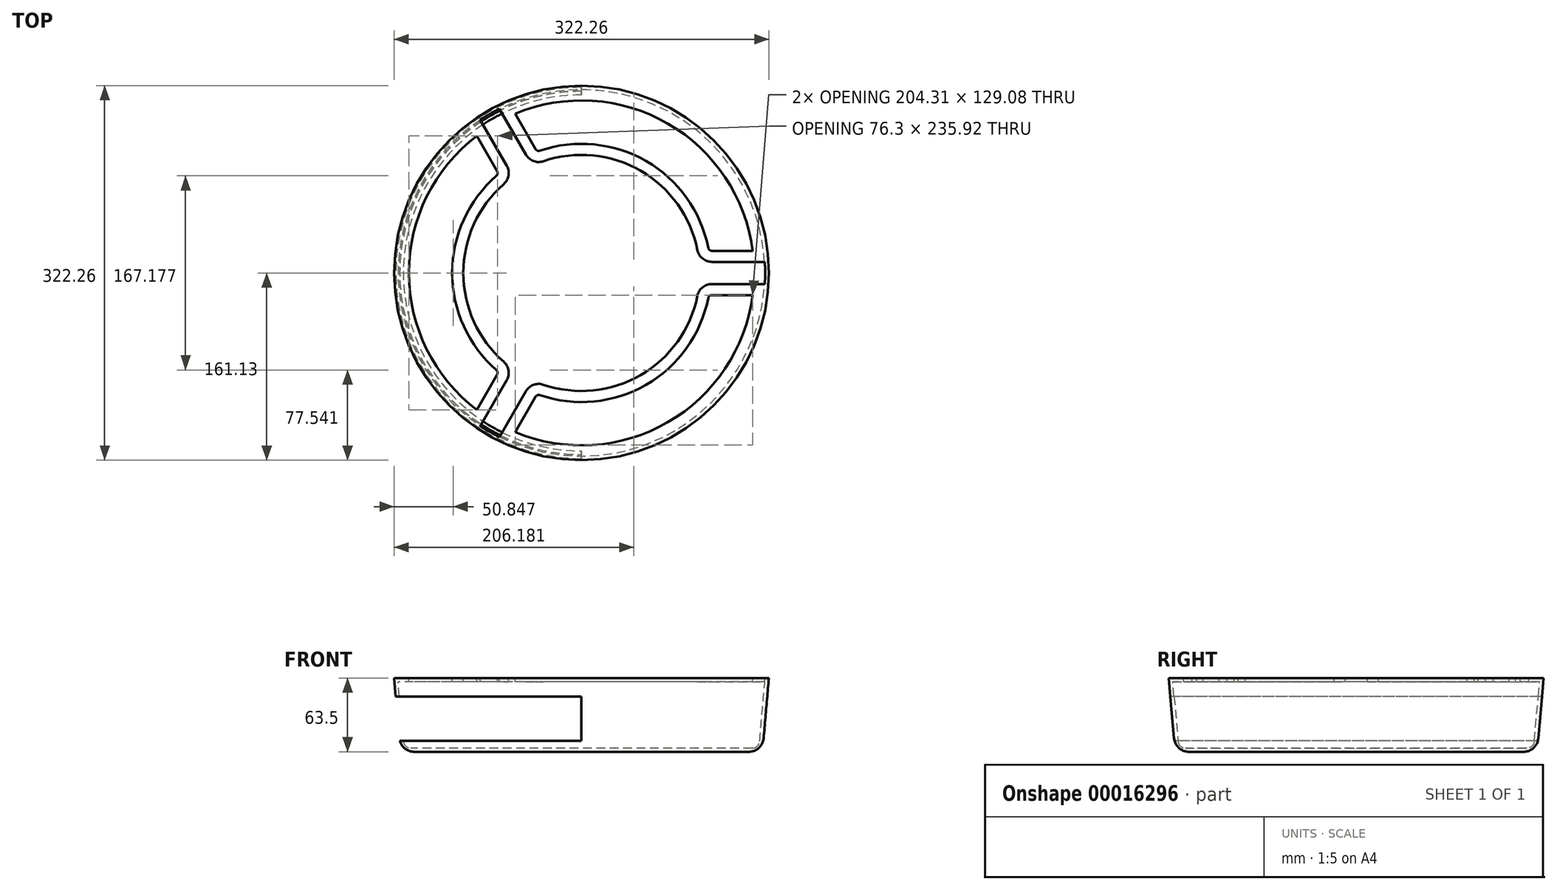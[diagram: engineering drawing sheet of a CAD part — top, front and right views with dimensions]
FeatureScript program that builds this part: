
annotation { "Feature Type Name" : "Feature", "Feature Type Description" : "" }
export const myFeature = defineFeature(function(context is Context, id is Id, definition is map)
    precondition{}
    {
        {
            var Q0;
            Q0=qCreatedBy(makeId("Top.planeOp"),FACE);
            var sketch = newSketch(context, id + "F0", { "sketchPlane" : qUnion([Q0])});
            skCircle(sketch, "E0", {"center": v(0, 0) * mm, "radius": 155.57 * mm});
            skSolve(sketch);
        }
        {
            var Q0;
            Q0 = qSketchRegion(id + "F0", true);
            extrude(context, id + "F1", {"entities" : qUnion([Q0]), "depth" : 63.5 * mm, "hasDraft" : true, "draftAngle" : 5 * degree});
        }
        {
            var Q0;
            Q0=makeQuery(id+"F1.opExtrude","CAP_FACE",FACE,{"disambiguationData":[OSD([sQuery(id+"F0.wireOp",EDGE,"E0")])],"isStart":false});
            shell(context, id + "F2", {"entities" : qUnion([Q0]), "thickness" : 3.17 * mm});
        }
        {
            var Q0;
            {var subQ0=sQuery(id+"F0.wireOp",EDGE,"E0");Q0=makeQuery(id+"F2.opShell","OFFSET_EDGE",EDGE,{"disambiguationData":[OSD([subQ0]),TDD([makeQuery(id+"F1.opExtrude","CAP_EDGE",EDGE,{"disambiguationData":[OSD([subQ0])],"isStart":true})])]});}
            fillet(context, id + "F3", {"entities" : qUnion([Q0]), "radius" : 6.35 * mm, "tangentPropagation" : true, "allowEdgeOverflow" : false});
        }
        {
            var Q0;
            Q0=makeQuery(id+"F1.opExtrude","CAP_EDGE",EDGE,{"disambiguationData":[OSD([sQuery(id+"F0.wireOp",EDGE,"E0")])],"isStart":true});
            fillet(context, id + "F4", {"entities" : qUnion([Q0]), "radius" : 12.7 * mm, "tangentPropagation" : true, "allowEdgeOverflow" : false});
        }
        {
            var Q0;
            Q0=makeQuery(id+"F1.opExtrude","CAP_FACE",FACE,{"disambiguationData":[OSD([sQuery(id+"F0.wireOp",EDGE,"E0")])],"isStart":false});
            var sketch = newSketch(context, id + "F5", { "sketchPlane" : qUnion([Q0])});
            skCircle(sketch, "E1", {"center": v(0, 0) * mm, "radius": 161.12 * mm});
            skLineSegment(sketch, "E2", {"start": v(161.12, 0) * mm, "end": v(161.13, 0) * mm});
            skLineSegment(sketch, "E3.1.0", {"start": v(-80.56, 139.54) * mm, "end": v(-80.57, 139.54) * mm});
            skLineSegment(sketch, "E3.2.0", {"start": v(-80.56, -139.54) * mm, "end": v(-80.57, -139.54) * mm});
            skArc(sketch, "E4", {"start": v(-66.94, 76.43) * mm, "mid": v(-101.6, 0) * mm, "end": v(-66.94, -76.43) * mm});
            skLineSegment(sketch, "E5.0", {"start": v(-47.81, 101.86) * mm, "end": v(-72.17, 144.06) * mm});
            skLineSegment(sketch, "E6.0", {"start": v(-64.3, 92.33) * mm, "end": v(-88.67, 134.53) * mm});
            skLineSegment(sketch, "E7.1.0", {"start": v(-64.3, -92.33) * mm, "end": v(-88.67, -134.53) * mm});
            skLineSegment(sketch, "E7.1.1", {"start": v(-47.81, -101.86) * mm, "end": v(-72.17, -144.06) * mm});
            skLineSegment(sketch, "E7.2.0", {"start": v(112.12, -9.52) * mm, "end": v(160.84, -9.52) * mm});
            skLineSegment(sketch, "E7.2.1", {"start": v(112.12, 9.52) * mm, "end": v(160.84, 9.52) * mm});
            skArc(sketch, "E8.trimOffspring", {"start": v(99.66, 19.76) * mm, "mid": v(50.8, 87.99) * mm, "end": v(-32.72, 96.19) * mm});
            skArc(sketch, "E9.trimOffspring", {"start": v(-32.72, -96.19) * mm, "mid": v(50.8, -87.99) * mm, "end": v(99.66, -19.76) * mm});
            skPoint(sketch, "E10.visualSharp", {"position": v(-58.83, -82.84) * mm});
            skArc(sketch, "E10.filletArc", {"start": v(-64.3, -92.33) * mm, "mid": v(-62.78, -83.91) * mm, "end": v(-66.94, -76.43) * mm});
            skPoint(sketch, "E11.visualSharp", {"position": v(101.15, -9.53) * mm});
            skArc(sketch, "E11.filletArc", {"start": v(112.12, -9.52) * mm, "mid": v(104.06, -12.41) * mm, "end": v(99.66, -19.76) * mm});
            skPoint(sketch, "E12.visualSharp", {"position": v(101.15, 9.52) * mm});
            skArc(sketch, "E12.filletArc", {"start": v(99.66, 19.76) * mm, "mid": v(104.06, 12.41) * mm, "end": v(112.12, 9.53) * mm});
            skPoint(sketch, "E13.visualSharp", {"position": v(-42.33, 92.36) * mm});
            skArc(sketch, "E13.filletArc", {"start": v(-47.81, 101.86) * mm, "mid": v(-41.28, 96.32) * mm, "end": v(-32.72, 96.19) * mm});
            skPoint(sketch, "E14.visualSharp", {"position": v(-58.83, 82.84) * mm});
            skArc(sketch, "E14.filletArc", {"start": v(-66.94, 76.43) * mm, "mid": v(-62.78, 83.91) * mm, "end": v(-64.3, 92.33) * mm});
            skPoint(sketch, "E15.visualSharp", {"position": v(-42.33, -92.36) * mm});
            skArc(sketch, "E15.filletArc", {"start": v(-32.72, -96.19) * mm, "mid": v(-41.28, -96.32) * mm, "end": v(-47.81, -101.86) * mm});
            skLineSegment(sketch, "E16.0", {"start": v(-72.56, 87.57) * mm, "end": v(-90.1, 117.96) * mm});
            skArc(sketch, "E16.1", {"start": v(-73.21, 83.6) * mm, "mid": v(-72.17, 85.47) * mm, "end": v(-72.56, 87.57) * mm});
            skArc(sketch, "E16.2", {"start": v(-73.21, 83.6) * mm, "mid": v(-111.13, 0) * mm, "end": v(-73.21, -83.6) * mm});
            skArc(sketch, "E16.3", {"start": v(-72.56, -87.57) * mm, "mid": v(-72.17, -85.47) * mm, "end": v(-73.21, -83.6) * mm});
            skLineSegment(sketch, "E16.4", {"start": v(-72.56, -87.57) * mm, "end": v(-90.1, -117.96) * mm});
            skLineSegment(sketch, "E17.0", {"start": v(-39.56, 106.62) * mm, "end": v(-57.1, 137) * mm});
            skArc(sketch, "E17.1", {"start": v(-39.56, 106.62) * mm, "mid": v(-37.93, 105.24) * mm, "end": v(-35.79, 105.2) * mm});
            skArc(sketch, "E17.2", {"start": v(109, 21.6) * mm, "mid": v(55.56, 96.24) * mm, "end": v(-35.79, 105.2) * mm});
            skArc(sketch, "E17.3", {"start": v(109, 21.6) * mm, "mid": v(110.1, 19.77) * mm, "end": v(112.12, 19.05) * mm});
            skLineSegment(sketch, "E17.4", {"start": v(112.12, 19.05) * mm, "end": v(147.2, 19.05) * mm});
            skLineSegment(sketch, "E18.0", {"start": v(112.12, -19.05) * mm, "end": v(147.2, -19.05) * mm});
            skArc(sketch, "E18.1", {"start": v(112.12, -19.05) * mm, "mid": v(110.1, -19.77) * mm, "end": v(109, -21.6) * mm});
            skArc(sketch, "E18.2", {"start": v(-35.79, -105.2) * mm, "mid": v(55.56, -96.24) * mm, "end": v(109, -21.6) * mm});
            skArc(sketch, "E18.3", {"start": v(-35.79, -105.2) * mm, "mid": v(-37.93, -105.24) * mm, "end": v(-39.56, -106.62) * mm});
            skLineSegment(sketch, "E18.4", {"start": v(-39.56, -106.62) * mm, "end": v(-57.1, -137) * mm});
            skArc(sketch, "E19.0", {"start": v(-90.1, 117.96) * mm, "mid": v(-148.43, 0) * mm, "end": v(-90.1, -117.96) * mm});
            skArc(sketch, "E20.trimOffspring", {"start": v(-65.82, 133.05) * mm, "mid": v(-74.22, 128.55) * mm, "end": v(-82.31, 123.52) * mm});
            skArc(sketch, "E21.trimOffspring", {"start": v(148.13, -9.52) * mm, "mid": v(148.43, 0) * mm, "end": v(148.13, 9.53) * mm});
            skArc(sketch, "E22.trimOffspring", {"start": v(147.2, 19.05) * mm, "mid": v(74.22, 128.55) * mm, "end": v(-57.1, 137) * mm});
            skArc(sketch, "E23.trimOffspring", {"start": v(-82.31, -123.52) * mm, "mid": v(-74.22, -128.55) * mm, "end": v(-65.82, -133.05) * mm});
            skLineSegment(sketch, "E24.trimOffspring", {"start": v(-63.5, 148.08) * mm, "end": v(-63.92, 148.82) * mm});
            skLineSegment(sketch, "E25.trimOffspring", {"start": v(160, 19.05) * mm, "end": v(160.84, 19.05) * mm});
            skLineSegment(sketch, "E26.trimOffspring", {"start": v(-96.5, -129.03) * mm, "end": v(-96.92, -129.77) * mm});
            skLineSegment(sketch, "E27.trimOffspring", {"start": v(-96.5, 129.03) * mm, "end": v(-96.92, 129.77) * mm});
            skArc(sketch, "E28.1.0", {"start": v(-57.1, -137) * mm, "mid": v(74.22, -128.55) * mm, "end": v(147.2, -19.05) * mm});
            skLineSegment(sketch, "E28.anchor1", {"start": v(0, 0) * mm, "end": v(-90.1, -117.96) * mm, "construction": true});
            skLineSegment(sketch, "E28.anchor2", {"start": v(0, 0) * mm, "end": v(147.2, -19.05) * mm, "construction": true});
            skLineSegment(sketch, "E29.trimOffspring", {"start": v(160, -19.05) * mm, "end": v(160.84, -19.05) * mm});
            skLineSegment(sketch, "E30.trimOffspring", {"start": v(-63.5, -148.08) * mm, "end": v(-63.92, -148.82) * mm});
            skSolve(sketch);
        }
        {
            var Q0;
            Q0=makeQuery(id+"F5.imprint","IMPRINT",FACE,{"disambiguationData":[TD([[makeQuery(id+"F5.imprint","IMPRINT",EDGE,{"derivedFrom":sQuery(id+"F5.wireOp",EDGE,"E4")}),-1.0]])]});
            var Q1;
            Q1=makeQuery(id+"F5.imprint","IMPRINT",FACE,{"disambiguationData":[TD([[makeQuery(id+"F5.imprint","IMPRINT",EDGE,{"derivedFrom":sQuery(id+"F5.wireOp",EDGE,"E8.trimOffspring")}),-1.0]])]});
            var Q2;
            Q2=makeQuery(id+"F5.imprint","IMPRINT",FACE,{"disambiguationData":[TD([[makeQuery(id+"F5.imprint","IMPRINT",EDGE,{"derivedFrom":sQuery(id+"F5.wireOp",EDGE,"E9.trimOffspring")}),-1.0]])]});
            extrude(context, id + "F6", {"entities" : qUnion([Q0, Q1, Q2]), "operationType" : NewBodyOperationType.ADD, "oppositeDirection" : true, "depth" : 3.17 * mm});
        }
        {
            var Q0;
            Q0=qCreatedBy(makeId("Right.planeOp"),FACE);
            var sketch = newSketch(context, id + "F7", { "sketchPlane" : qUnion([Q0])});
            skLineSegment(sketch, "E31.bottom", {"start": v(183.82, 47.62) * mm, "end": v(-185.56, 47.62) * mm});
            skLineSegment(sketch, "E31.top", {"start": v(183.82, 9.53) * mm, "end": v(-185.56, 9.53) * mm});
            skLineSegment(sketch, "E31.left", {"start": v(183.82, 47.62) * mm, "end": v(183.82, 9.52) * mm});
            skLineSegment(sketch, "E31.right", {"start": v(-185.56, 47.62) * mm, "end": v(-185.56, 9.52) * mm});
            skSolve(sketch);
        }
        {
            var Q0;
            Q0=makeQuery(id+"F7.imprint","IMPRINT",FACE,{"disambiguationData":[TD([[makeQuery(id+"F7.imprint","IMPRINT",EDGE,{"derivedFrom":sQuery(id+"F7.wireOp",EDGE,"E31.bottom")}),1.0]])]});
            extrude(context, id + "F8", {"entities" : qUnion([Q0]), "operationType" : NewBodyOperationType.REMOVE, "endBound" : BoundingType.THROUGH_ALL, "oppositeDirection" : true, "depth" : 25.4 * mm});
        }
    });
